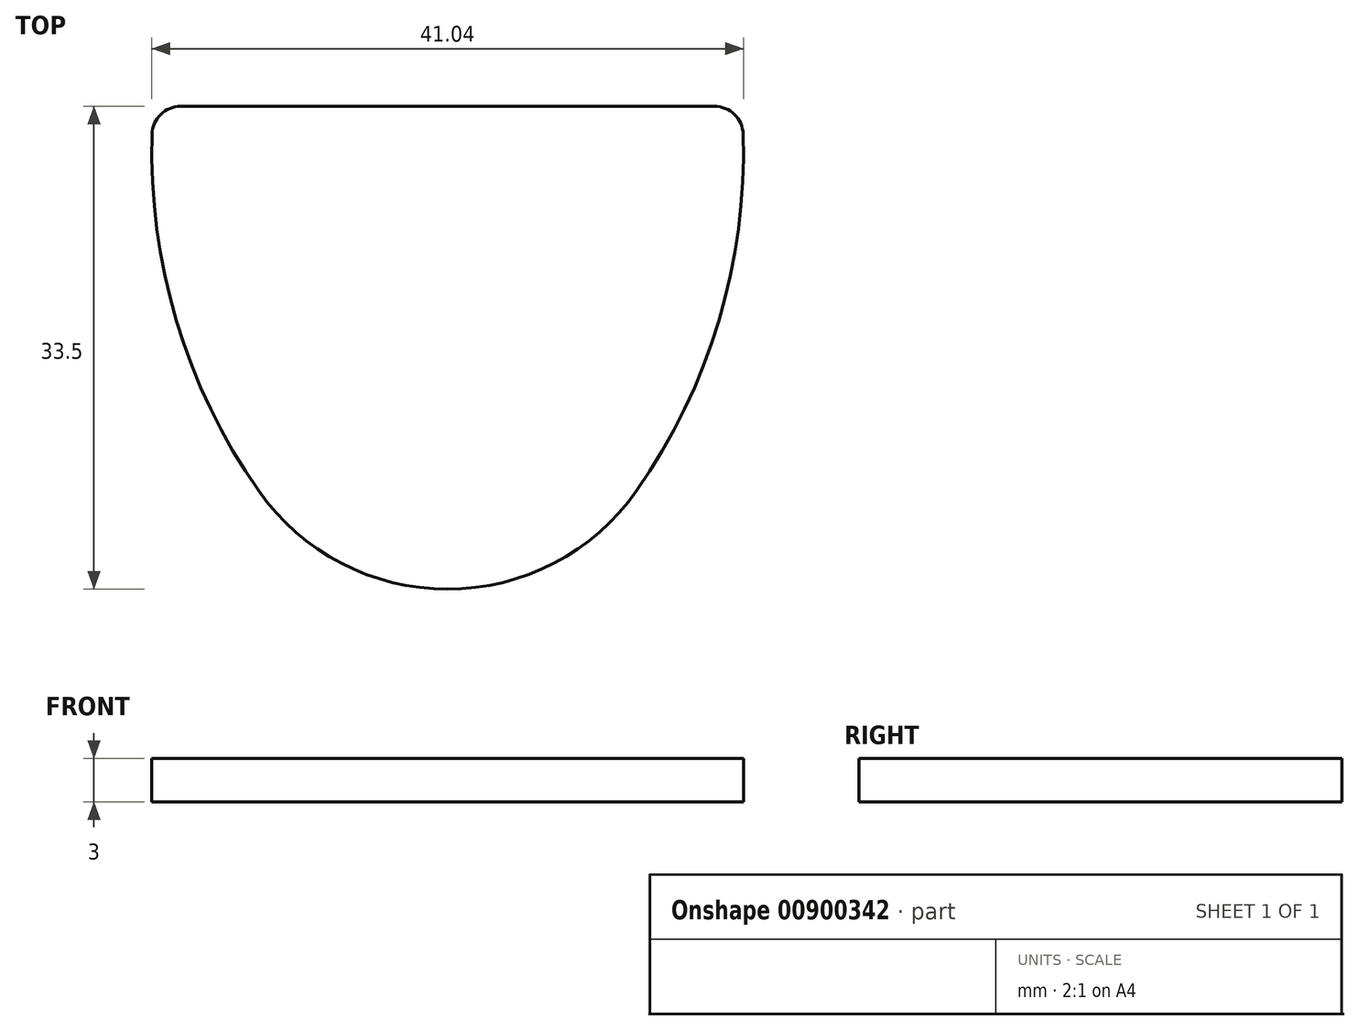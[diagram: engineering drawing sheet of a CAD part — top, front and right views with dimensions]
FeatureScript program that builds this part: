
annotation { "Feature Type Name" : "Feature", "Feature Type Description" : "" }
export const myFeature = defineFeature(function(context is Context, id is Id, definition is map)
    precondition{}
    {
        {
            var Q0;
            Q0=qCreatedBy(makeId("Top.planeOp"),FACE);
            var sketch = newSketch(context, id + "F0", { "sketchPlane" : qUnion([Q0])});
            skLineSegment(sketch, "E0", {"start": v(-18.5, 0) * mm, "end": v(0, 0) * mm});
            skLineSegment(sketch, "E1", {"start": v(0, 0) * mm, "end": v(18.5, 0) * mm});
            skArc(sketch, "E2", {"start": v(13.1, -26.67) * mm, "mid": v(18.8, -14.9) * mm, "end": v(20.5, -1.94) * mm});
            skArc(sketch, "E3", {"start": v(-20.5, -1.94) * mm, "mid": v(-18.8, -14.9) * mm, "end": v(-13.1, -26.67) * mm});
            skArc(sketch, "E4", {"start": v(-13.1, -26.67) * mm, "mid": v(0, -33.5) * mm, "end": v(13.1, -26.67) * mm});
            skPoint(sketch, "E5.visualSharp", {"position": v(-20.4, 0) * mm});
            skArc(sketch, "E5.filletArc", {"start": v(-18.5, 0) * mm, "mid": v(-19.9, -0.56) * mm, "end": v(-20.5, -1.94) * mm});
            skPoint(sketch, "E6.visualSharp", {"position": v(20.4, 0) * mm});
            skArc(sketch, "E6.filletArc", {"start": v(20.5, -1.94) * mm, "mid": v(19.9, -0.56) * mm, "end": v(18.5, 0) * mm});
            skPoint(sketch, "E7", {"position": v(0, -14) * mm});
            skCircle(sketch, "E8", {"center": v(-18.5, -2) * mm, "radius": 2 * mm, "construction": true});
            skLineSegment(sketch, "E9.bottom", {"start": v(25.3, 14.77) * mm, "end": v(-25.3, 14.77) * mm, "construction": true});
            skLineSegment(sketch, "E9.top", {"start": v(25.3, -42.77) * mm, "end": v(-25.3, -42.77) * mm, "construction": true});
            skLineSegment(sketch, "E9.left", {"start": v(25.3, 14.77) * mm, "end": v(25.3, -42.77) * mm, "construction": true});
            skLineSegment(sketch, "E9.right", {"start": v(-25.3, 14.77) * mm, "end": v(-25.3, -42.77) * mm, "construction": true});
            skSolve(sketch);
        }
        {
            var Q0;
            Q0=qSketchRegion(id+"F0",true);
            extrude(context, id + "F1", {"entities" : qUnion([Q0]), "depth" : 3 * mm, "offsetDistance" : 25 * mm});
        }
    });
